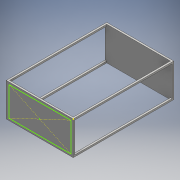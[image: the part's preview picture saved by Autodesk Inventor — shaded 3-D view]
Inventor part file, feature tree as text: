
AUTODESK INVENTOR PART (.ipt)
format: ipt  version: 2016 (Build 200138000, 138)  size: 125,952 bytes
history: native  units: mm
features: sketch x4, extrude x3
ambient origin geometry x8: Origin, YZ Plane, XZ Plane, XY Plane, X Axis, Y Axis, Z Axis, Center Point
bodies: Solid1 (feature_tree)
feature tree (7):
  extrude  "Extrusion1"  Depth=200.0mm
  extrude  "Extrusion2"  Depth=5.0mm
  extrude  "Extrusion3"  Depth=5.0mm
  sketch  "Sketch5"  dims[d9=5.0mm d10=5.0mm]
  sketch  "Sketch6"  dims[d11=5.0mm d12=10.0mm d13=0.0mm d14=5.0mm d15=5.0mm d16=5.0mm d17=5.0mm d18=10.0mm d19=0.0mm]
  sketch  "Sketch3"  dims[d0=100.0mm d1=200.0mm]
  sketch  "Sketch4"  dims[d6=300.0mm d7=0.0mm d8=5.0mm]
